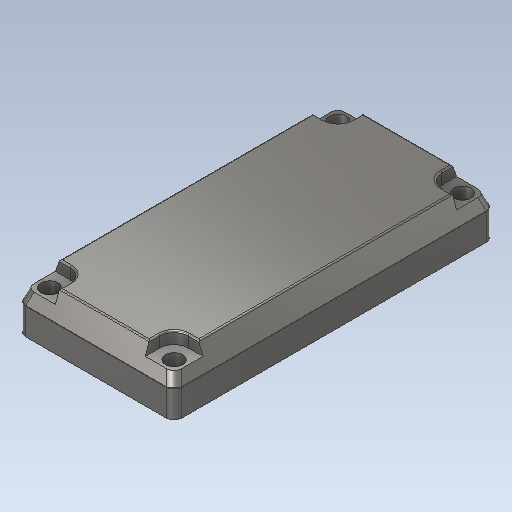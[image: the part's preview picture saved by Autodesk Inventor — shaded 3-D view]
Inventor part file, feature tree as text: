
AUTODESK INVENTOR PART (.ipt)
format: ipt  version: 2020 (Build 240168000, 168)  size: 269,312 bytes
history: native  units: mm
features: other x4, mirror x4, chamfer x4, extrude x3, fillet x2, sketch x2
ambient origin geometry x8: Origin, YZ Plane, XZ Plane, XY Plane, X Axis, Y Axis, Z Axis, Center Point
bodies: Body1 (feature_tree)
feature tree (19):
  other  "Sólido1"
  extrude  "Extrusión1"  Depth=40.6mm
  extrude  "Extrusión2"  Depth=0.2mm
  mirror  "Simetría1"
  mirror  "Simetría2"
  extrude  "Extrusión3"  Depth=0.2mm TaperAngle=0.0deg
  mirror  "Simetría3"
  mirror  "Simetría4"
  chamfer  "Chaflán1"  Distance=2.2mm
  chamfer  "Chaflán2"  Distance=2.2mm
  chamfer  "Chaflán3"  Distance=2.2mm
  chamfer  "Chaflán4"  Distance=1.5mm
  fillet  "Empalme1"  Radius=2.0mm
  fillet  "Empalme2"  Radius=2.0mm
  sketch  "Boceto1"  dims[d0=19.8mm d1=40.6mm]
  other  "Eje de trabajo1"
  other  "Eje de trabajo2"
  other  "Eje de trabajo3"
  sketch  "Boceto4"  dims[d2=6.4mm d3=0.0mm d6=3.6mm d8=1.5mm d9=0.0mm d10=2.2mm d11=2.2mm d12=2.2mm d13=1.5mm d14=0.0mm d15=3.0mm d16=2.0mm d17=3.490659mm d18=3.0mm d19=2.0mm d20=3.490659mm d21=3.0mm d22=2.0mm d23=3.490659mm d24=3.0mm d25=2.0mm d26=3.490659mm d27=1.0mm d28=0.2mm]
